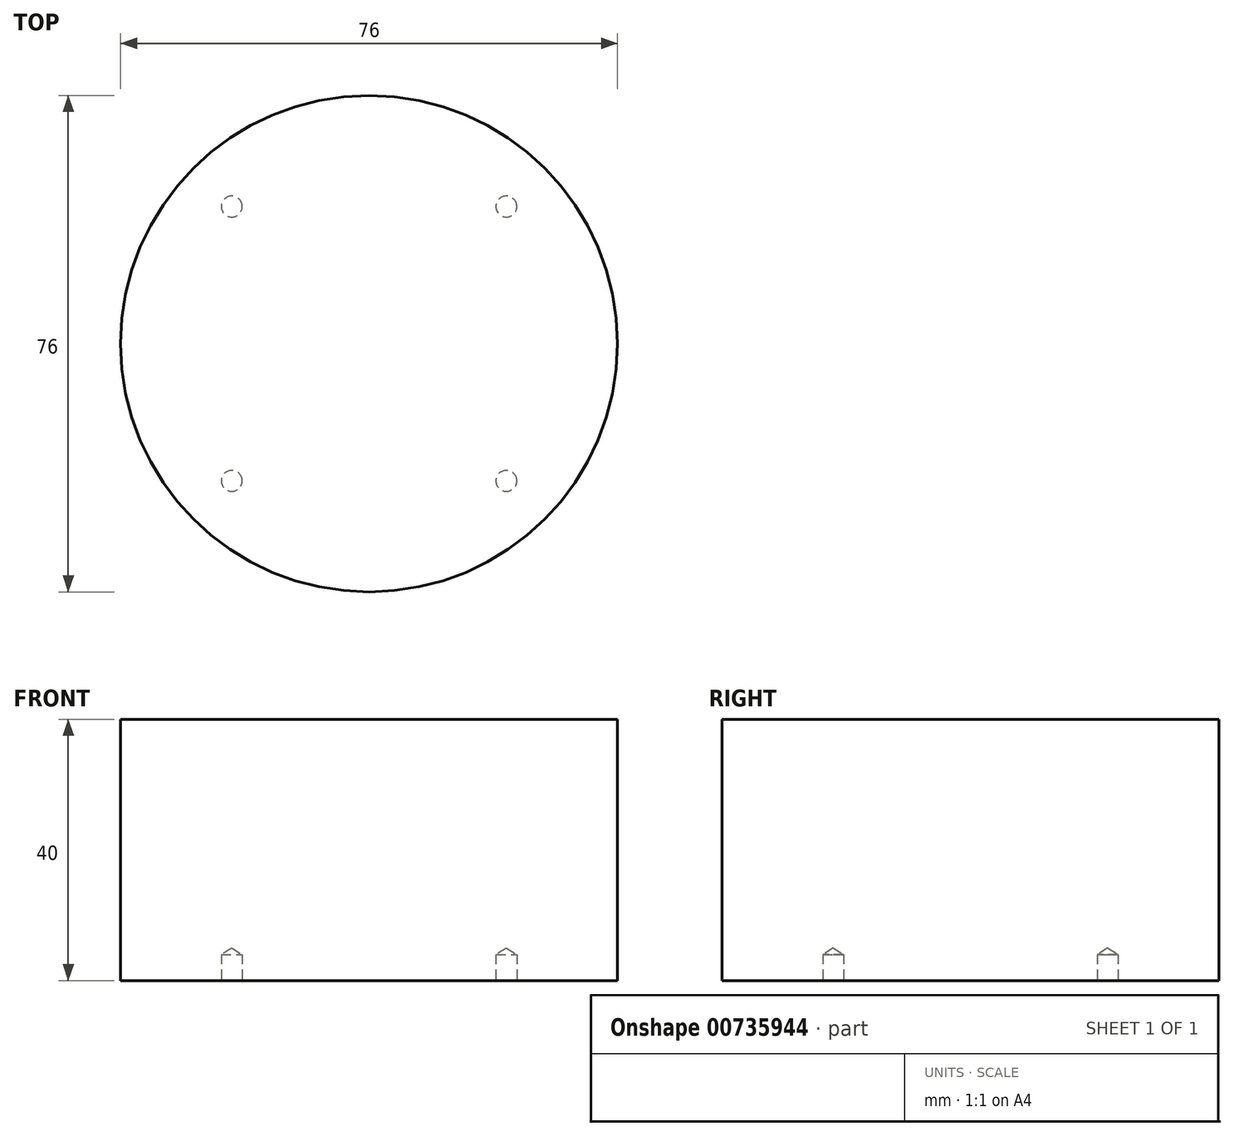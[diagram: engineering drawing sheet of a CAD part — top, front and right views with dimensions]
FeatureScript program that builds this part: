
annotation { "Feature Type Name" : "Feature", "Feature Type Description" : "" }
export const myFeature = defineFeature(function(context is Context, id is Id, definition is map)
    precondition{}
    {
        {
            var Q0;
            Q0=qCreatedBy(makeId("Top.planeOp"),FACE);
            var sketch = newSketch(context, id + "F0", { "sketchPlane" : qUnion([Q0])});
            skCircle(sketch, "E0", {"center": v(0, 0) * mm, "radius": 38 * mm});
            skSolve(sketch);
        }
        {
            var Q0;
            Q0=makeQuery(id+"F0.imprint","IMPRINT",FACE,{"disambiguationData":[TD([[makeQuery(id+"F0.imprint","IMPRINT",EDGE,{"derivedFrom":sQuery(id+"F0.wireOp",EDGE,"E0")}),1.0]])]});
            extrude(context, id + "F1", {"entities" : qUnion([Q0]), "depth" : 40 * mm, "offsetDistance" : 25 * mm});
        }
        {
            var Q0;
            Q0=makeQuery(id+"F1.opExtrude","CAP_FACE",FACE,{"disambiguationData":[OSD([sQuery(id+"F0.wireOp",EDGE,"E0")])],"isStart":true});
            var sketch = newSketch(context, id + "F2", { "sketchPlane" : qUnion([Q0])});
            skLineSegment(sketch, "E1.bottom", {"start": v(21, -21) * mm, "end": v(-21, -21) * mm, "construction": true});
            skLineSegment(sketch, "E1.top", {"start": v(21, 21) * mm, "end": v(-21, 21) * mm, "construction": true});
            skLineSegment(sketch, "E1.left", {"start": v(21, -21) * mm, "end": v(21, 21) * mm, "construction": true});
            skLineSegment(sketch, "E1.right", {"start": v(-21, -21) * mm, "end": v(-21, 21) * mm, "construction": true});
            skPoint(sketch, "E1.middle", {"position": v(0, 0) * mm});
            skSolve(sketch);
        }
        {
            var Q0;
            Q0=sQuery(id+"F2.wireOp",VERTEX,"E1.top.end");
            var Q1;
            Q1=sQuery(id+"F2.wireOp",VERTEX,"E1.top.start");
            var Q2;
            Q2=sQuery(id+"F2.wireOp",VERTEX,"E1.bottom.start");
            var Q3;
            Q3=sQuery(id+"F2.wireOp",VERTEX,"E1.bottom.end");
            var Q4;
            Q4=makeQuery(id+"F1.opExtrude","SWEPT_BODY",BODY,{"disambiguationData":[OSD([sQuery(id+"F0.wireOp",EDGE,"E0")])]});
            hole(context, id + "F3", {"style" : HoleStyle.SIMPLE, "endStyle" : HoleEndStyle.BLIND, "holeDiameter" : 3.2 * mm, "majorDiameter" : 5 * mm, "holeDepth" : 4 * mm, "isTappedThrough" : true, "tappedDepth" : 2.3 * mm, "tapClearance" : 3, "startFromSketch" : true, "locations" : qUnion([Q0, Q1, Q2, Q3]), "scope" : qUnion([Q4])});
        }
    });
